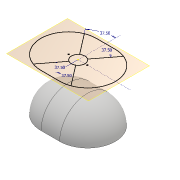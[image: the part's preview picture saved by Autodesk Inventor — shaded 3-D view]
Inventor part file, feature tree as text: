
AUTODESK INVENTOR PART (.ipt)
format: ipt  version: 2018 (Build 220112000, 112)  size: 125,952 bytes
history: native  units: mm
features: sketch x2, revolve x1, plane x1
ambient origin geometry x8: Origin, YZ Plane, XZ Plane, XY Plane, X Axis, Y Axis, Z Axis, Center Point
bodies: Solid1 (feature_tree)
feature tree (4):
  revolve  "Revolution1"  [1 undecoded]
  plane  "Work Plane2"
  sketch  "Sketch3"  dims[d2=180.0deg d3=12.5mm d7=70.0mm d14=6.544985mm d15=6.544985mm d16=6.544985mm d17=6.544985mm]
  sketch  "Sketch1"  dims[d0=25.0mm d1=75.0mm]
note: 1 required parameter value undecoded (feature->parameter linkage not recoverable at this tier; creation-order binding heuristic only, values carry confidence <= 0.55)
